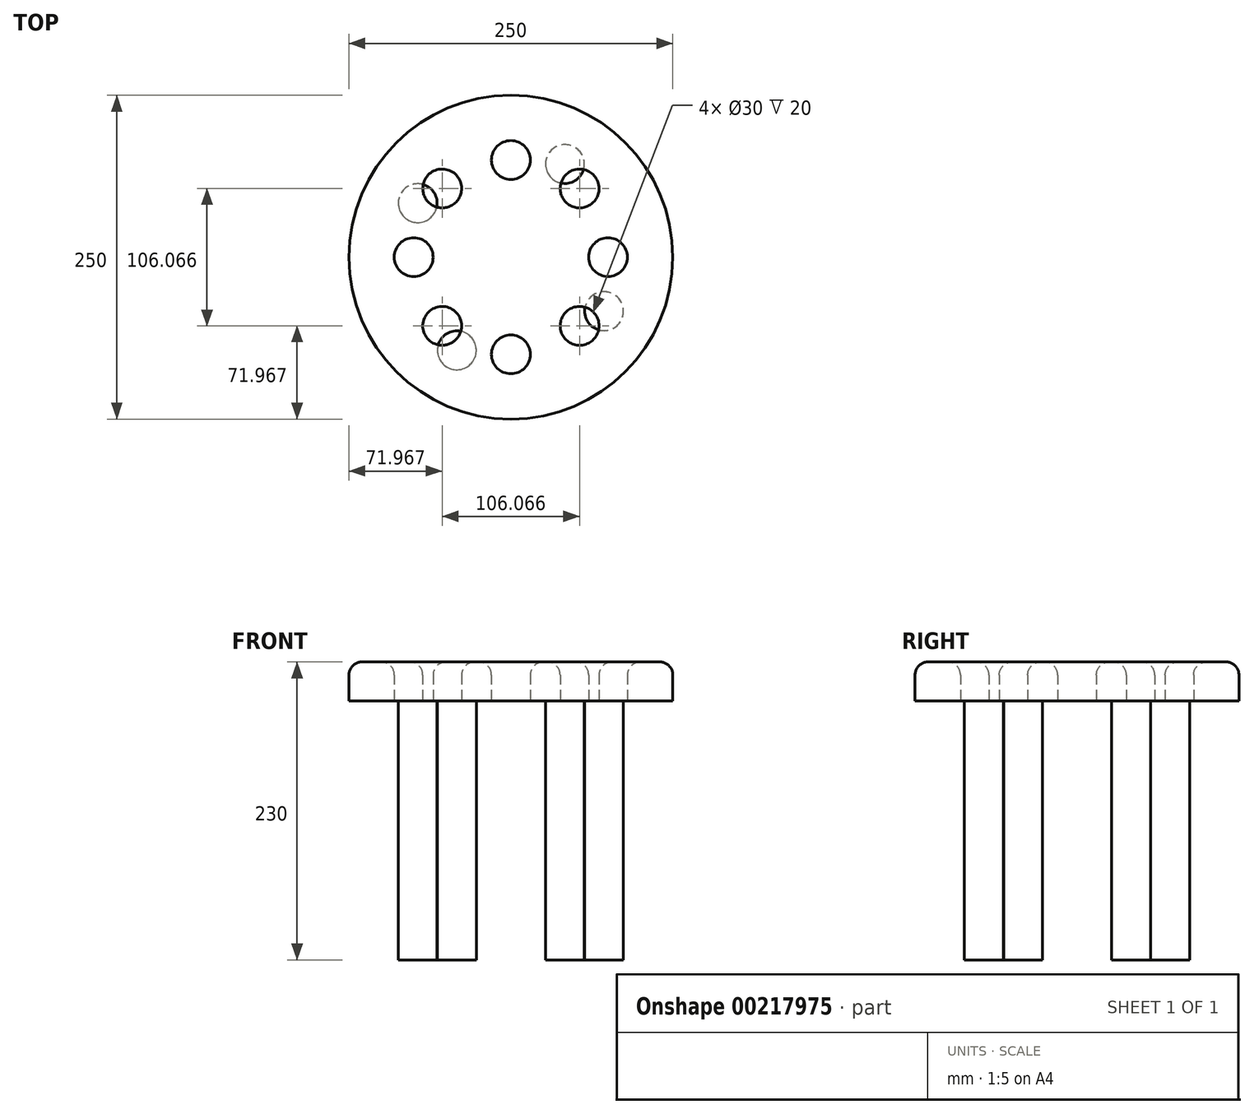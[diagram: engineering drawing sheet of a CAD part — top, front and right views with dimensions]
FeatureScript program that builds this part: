
annotation { "Feature Type Name" : "Feature", "Feature Type Description" : "" }
export const myFeature = defineFeature(function(context is Context, id is Id, definition is map)
    precondition{}
    {
        {
            var Q0;
            Q0=qCreatedBy(makeId("Top.planeOp"),FACE);
            var sketch = newSketch(context, id + "F0", { "sketchPlane" : qUnion([Q0])});
            skCircle(sketch, "E0", {"center": v(0, 0) * mm, "radius": 125 * mm});
            skSolve(sketch);
        }
        {
            var Q0;
            Q0=makeQuery(id+"F0.imprint","IMPRINT",FACE,{"disambiguationData":[TD([[makeQuery(id+"F0.imprint","IMPRINT",EDGE,{"derivedFrom":sQuery(id+"F0.wireOp",EDGE,"E0")}),1.0]])]});
            var sketch = newSketch(context, id + "F1", { "sketchPlane" : qUnion([Q0])});
            skCircle(sketch, "E1", {"center": v(0, 75) * mm, "radius": 15 * mm});
            skCircle(sketch, "E2.1.0", {"center": v(-53.03, 53.03) * mm, "radius": 15 * mm});
            skCircle(sketch, "E2.2.0", {"center": v(-75, 0) * mm, "radius": 15 * mm});
            skCircle(sketch, "E2.3.0", {"center": v(-53.03, -53.03) * mm, "radius": 15 * mm});
            skCircle(sketch, "E2.4.0", {"center": v(0, -75) * mm, "radius": 15 * mm});
            skCircle(sketch, "E2.5.0", {"center": v(53.03, -53.03) * mm, "radius": 15 * mm});
            skCircle(sketch, "E2.6.0", {"center": v(75, 0) * mm, "radius": 15 * mm});
            skCircle(sketch, "E2.7.0", {"center": v(53.03, 53.03) * mm, "radius": 15 * mm});
            skPoint(sketch, "E2.center", {"position": v(0, 0) * mm});
            skSolve(sketch);
        }
        {
            var Q0;
            Q0 = qSketchRegion(id + "F0", true);
            extrude(context, id + "F2", {"entities" : qUnion([Q0]), "depth" : 30 * mm});
        }
        {
            var Q0;
            Q0 = qSketchRegion(id + "F1", true);
            extrude(context, id + "F3", {"entities" : qUnion([Q0]), "operationType" : NewBodyOperationType.REMOVE, "depth" : 265 * mm});
        }
        {
            var Q0;
            Q0=makeQuery(id+"F2.opExtrude","CAP_FACE",FACE,{"disambiguationData":[OSD([sQuery(id+"F0.wireOp",EDGE,"E0")])],"isStart":false});
            fillet(context, id + "F4", {"entities" : qUnion([Q0]), "radius" : 10 * mm, "tangentPropagation" : true, "allowEdgeOverflow" : false});
        }
        {
            var Q0;
            Q0=makeQuery(id+"F2.opExtrude","CAP_FACE",FACE,{"disambiguationData":[OSD([sQuery(id+"F0.wireOp",EDGE,"E0")])],"isStart":true});
            var sketch = newSketch(context, id + "F5", { "sketchPlane" : qUnion([Q0])});
            skCircle(sketch, "E3", {"center": v(-41.7, 71.91) * mm, "radius": 15 * mm});
            skCircle(sketch, "E4.1.0", {"center": v(-71.91, -41.7) * mm, "radius": 15 * mm});
            skCircle(sketch, "E4.2.0", {"center": v(41.7, -71.91) * mm, "radius": 15 * mm});
            skCircle(sketch, "E4.3.0", {"center": v(71.91, 41.7) * mm, "radius": 15 * mm});
            skPoint(sketch, "E4.center", {"position": v(0, 0) * mm});
            skSolve(sketch);
        }
        {
            var Q0;
            Q0 = qSketchRegion(id + "F5", true);
            extrude(context, id + "F6", {"entities" : qUnion([Q0]), "operationType" : NewBodyOperationType.ADD, "depth" : 200 * mm});
        }
    });
